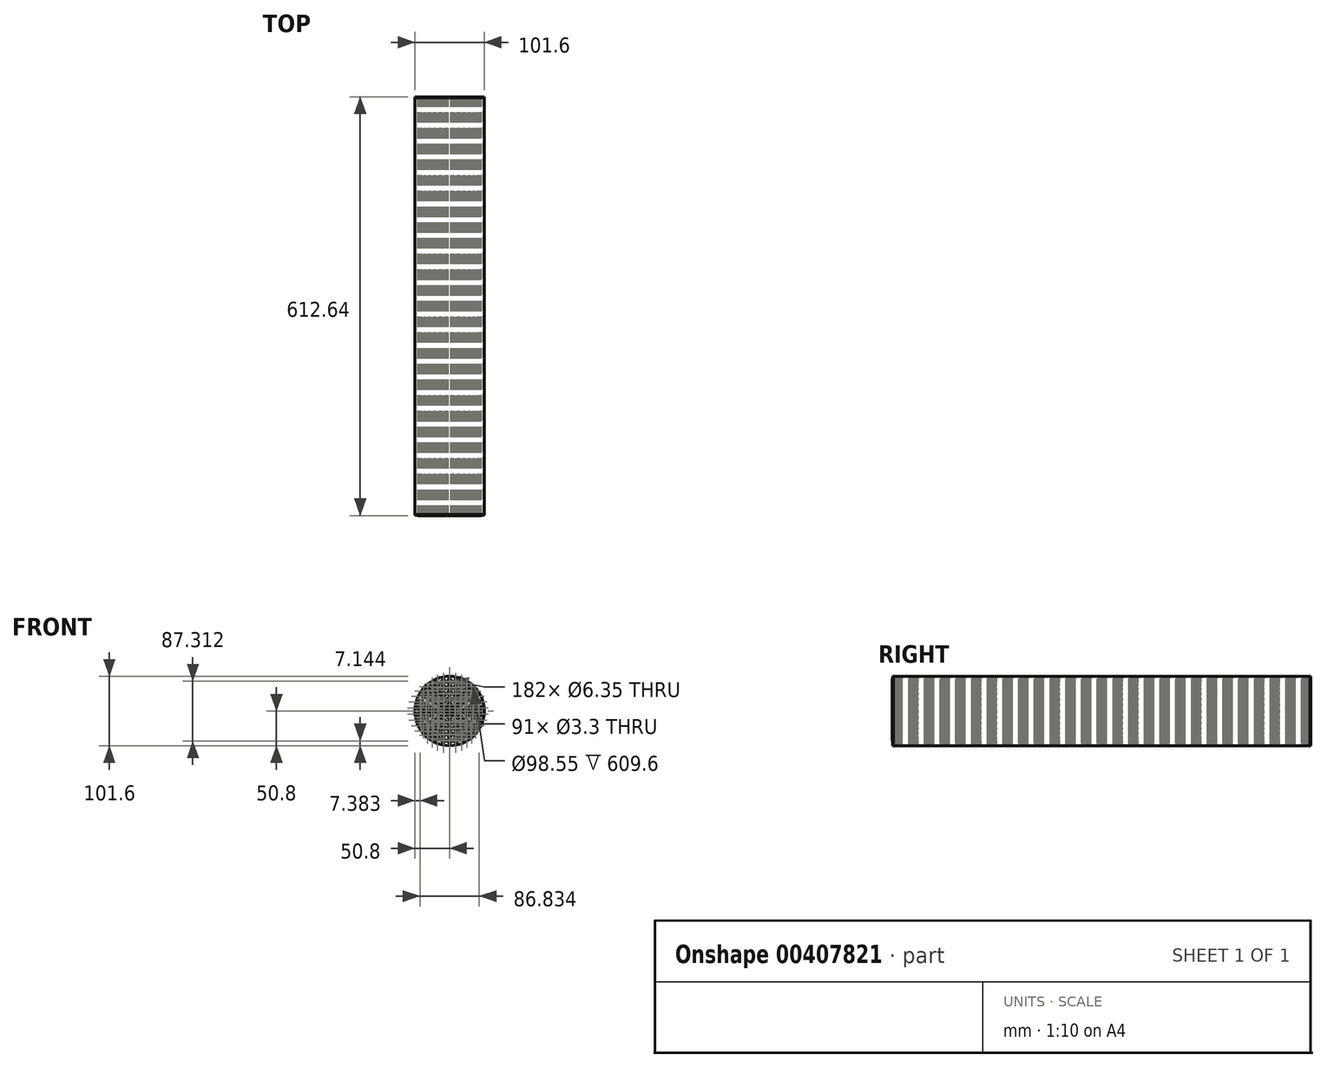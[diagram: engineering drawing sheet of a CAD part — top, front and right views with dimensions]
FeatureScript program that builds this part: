
annotation { "Feature Type Name" : "Feature", "Feature Type Description" : "" }
export const myFeature = defineFeature(function(context is Context, id is Id, definition is map)
    precondition{}
    {
        {
            var Q0;
            Q0=qCreatedBy(makeId("Front.planeOp"),FACE);
            var sketch = newSketch(context, id + "F0", { "sketchPlane" : qUnion([Q0])});
            skCircle(sketch, "E0", {"center": v(0, 0) * mm, "radius": 50.8 * mm});
            skCircle(sketch, "E1", {"center": v(0, 0) * mm, "radius": 3.18 * mm});
            skCircle(sketch, "E2", {"center": v(0, 8.73) * mm, "radius": 3.18 * mm});
            skCircle(sketch, "E3", {"center": v(0, 17.46) * mm, "radius": 3.18 * mm});
            skCircle(sketch, "E4", {"center": v(0, 26.2) * mm, "radius": 3.18 * mm});
            skCircle(sketch, "E5", {"center": v(0, 34.93) * mm, "radius": 3.18 * mm});
            skCircle(sketch, "E6", {"center": v(0, 43.66) * mm, "radius": 3.18 * mm});
            skCircle(sketch, "E7.0", {"center": v(0, 0) * mm, "radius": 49.28 * mm});
            skCircle(sketch, "E8.1.0", {"center": v(-7.56, 4.37) * mm, "radius": 3.18 * mm});
            skCircle(sketch, "E8.2.0", {"center": v(-7.56, -4.37) * mm, "radius": 3.18 * mm});
            skCircle(sketch, "E8.3.0", {"center": v(0, -8.73) * mm, "radius": 3.18 * mm});
            skCircle(sketch, "E8.4.0", {"center": v(7.56, -4.37) * mm, "radius": 3.18 * mm});
            skCircle(sketch, "E8.5.0", {"center": v(7.56, 4.37) * mm, "radius": 3.18 * mm});
            skCircle(sketch, "E9.1.0", {"center": v(-8.73, 15.12) * mm, "radius": 3.18 * mm});
            skCircle(sketch, "E9.2.0", {"center": v(-15.12, 8.73) * mm, "radius": 3.18 * mm});
            skCircle(sketch, "E9.3.0", {"center": v(-17.46, 0) * mm, "radius": 3.18 * mm});
            skCircle(sketch, "E9.4.0", {"center": v(-15.12, -8.73) * mm, "radius": 3.18 * mm});
            skCircle(sketch, "E9.5.0", {"center": v(-8.73, -15.12) * mm, "radius": 3.18 * mm});
            skCircle(sketch, "E9.6.0", {"center": v(0, -17.46) * mm, "radius": 3.18 * mm});
            skCircle(sketch, "E9.7.0", {"center": v(8.73, -15.12) * mm, "radius": 3.18 * mm});
            skCircle(sketch, "E9.8.0", {"center": v(15.12, -8.73) * mm, "radius": 3.18 * mm});
            skCircle(sketch, "E9.9.0", {"center": v(17.46, 0) * mm, "radius": 3.18 * mm});
            skCircle(sketch, "E9.10.0", {"center": v(15.12, 8.73) * mm, "radius": 3.18 * mm});
            skCircle(sketch, "E9.11.0", {"center": v(8.73, 15.12) * mm, "radius": 3.18 * mm});
            skCircle(sketch, "E10.1.0", {"center": v(-8.96, 24.61) * mm, "radius": 3.17 * mm});
            skCircle(sketch, "E10.2.0", {"center": v(-16.84, 20.07) * mm, "radius": 3.18 * mm});
            skCircle(sketch, "E10.3.0", {"center": v(-22.68, 13.1) * mm, "radius": 3.18 * mm});
            skCircle(sketch, "E10.4.0", {"center": v(-25.8, 4.55) * mm, "radius": 3.18 * mm});
            skCircle(sketch, "E10.5.0", {"center": v(-25.8, -4.55) * mm, "radius": 3.18 * mm});
            skCircle(sketch, "E10.6.0", {"center": v(-22.68, -13.1) * mm, "radius": 3.18 * mm});
            skCircle(sketch, "E10.7.0", {"center": v(-16.84, -20.07) * mm, "radius": 3.17 * mm});
            skCircle(sketch, "E10.8.0", {"center": v(-8.96, -24.61) * mm, "radius": 3.18 * mm});
            skCircle(sketch, "E10.9.0", {"center": v(0, -26.2) * mm, "radius": 3.17 * mm});
            skCircle(sketch, "E10.10.0", {"center": v(8.96, -24.61) * mm, "radius": 3.18 * mm});
            skCircle(sketch, "E10.11.0", {"center": v(16.84, -20.07) * mm, "radius": 3.18 * mm});
            skCircle(sketch, "E10.12.0", {"center": v(22.68, -13.1) * mm, "radius": 3.17 * mm});
            skCircle(sketch, "E10.13.0", {"center": v(25.8, -4.55) * mm, "radius": 3.17 * mm});
            skCircle(sketch, "E10.14.0", {"center": v(25.8, 4.55) * mm, "radius": 3.18 * mm});
            skCircle(sketch, "E10.15.0", {"center": v(22.68, 13.1) * mm, "radius": 3.18 * mm});
            skCircle(sketch, "E10.16.0", {"center": v(16.84, 20.07) * mm, "radius": 3.18 * mm});
            skCircle(sketch, "E10.17.0", {"center": v(8.96, 24.61) * mm, "radius": 3.18 * mm});
            skCircle(sketch, "E11.1.0", {"center": v(-9.04, 33.73) * mm, "radius": 3.18 * mm});
            skCircle(sketch, "E11.2.0", {"center": v(-17.46, 30.25) * mm, "radius": 3.18 * mm});
            skCircle(sketch, "E11.3.0", {"center": v(-24.7, 24.7) * mm, "radius": 3.18 * mm});
            skCircle(sketch, "E11.4.0", {"center": v(-30.25, 17.46) * mm, "radius": 3.18 * mm});
            skCircle(sketch, "E11.5.0", {"center": v(-33.73, 9.04) * mm, "radius": 3.18 * mm});
            skCircle(sketch, "E11.6.0", {"center": v(-34.93, 0) * mm, "radius": 3.18 * mm});
            skCircle(sketch, "E11.7.0", {"center": v(-33.73, -9.04) * mm, "radius": 3.18 * mm});
            skCircle(sketch, "E11.8.0", {"center": v(-30.25, -17.46) * mm, "radius": 3.18 * mm});
            skCircle(sketch, "E11.9.0", {"center": v(-24.7, -24.7) * mm, "radius": 3.18 * mm});
            skCircle(sketch, "E11.10.0", {"center": v(-17.46, -30.25) * mm, "radius": 3.18 * mm});
            skCircle(sketch, "E11.11.0", {"center": v(-9.04, -33.73) * mm, "radius": 3.18 * mm});
            skCircle(sketch, "E11.12.0", {"center": v(0, -34.93) * mm, "radius": 3.18 * mm});
            skCircle(sketch, "E11.13.0", {"center": v(9.04, -33.73) * mm, "radius": 3.18 * mm});
            skCircle(sketch, "E11.14.0", {"center": v(17.46, -30.25) * mm, "radius": 3.18 * mm});
            skCircle(sketch, "E11.15.0", {"center": v(24.7, -24.7) * mm, "radius": 3.18 * mm});
            skCircle(sketch, "E11.16.0", {"center": v(30.25, -17.46) * mm, "radius": 3.18 * mm});
            skCircle(sketch, "E11.17.0", {"center": v(33.73, -9.04) * mm, "radius": 3.18 * mm});
            skCircle(sketch, "E11.18.0", {"center": v(34.93, 0) * mm, "radius": 3.18 * mm});
            skCircle(sketch, "E11.19.0", {"center": v(33.73, 9.04) * mm, "radius": 3.18 * mm});
            skCircle(sketch, "E11.20.0", {"center": v(30.25, 17.46) * mm, "radius": 3.18 * mm});
            skCircle(sketch, "E11.21.0", {"center": v(24.7, 24.7) * mm, "radius": 3.18 * mm});
            skCircle(sketch, "E11.22.0", {"center": v(17.46, 30.25) * mm, "radius": 3.18 * mm});
            skCircle(sketch, "E11.23.0", {"center": v(9.04, 33.73) * mm, "radius": 3.18 * mm});
            skCircle(sketch, "E12.1.0", {"center": v(-9.08, 42.7) * mm, "radius": 3.18 * mm});
            skCircle(sketch, "E12.2.0", {"center": v(-17.76, 39.88) * mm, "radius": 3.18 * mm});
            skCircle(sketch, "E12.3.0", {"center": v(-25.66, 35.32) * mm, "radius": 3.18 * mm});
            skCircle(sketch, "E12.4.0", {"center": v(-32.44, 29.21) * mm, "radius": 3.17 * mm});
            skCircle(sketch, "E12.5.0", {"center": v(-37.8, 21.83) * mm, "radius": 3.18 * mm});
            skCircle(sketch, "E12.6.0", {"center": v(-41.52, 13.5) * mm, "radius": 3.18 * mm});
            skCircle(sketch, "E12.7.0", {"center": v(-43.42, 4.56) * mm, "radius": 3.18 * mm});
            skCircle(sketch, "E12.8.0", {"center": v(-43.42, -4.56) * mm, "radius": 3.18 * mm});
            skCircle(sketch, "E12.9.0", {"center": v(-41.52, -13.5) * mm, "radius": 3.18 * mm});
            skCircle(sketch, "E12.10.0", {"center": v(-37.8, -21.83) * mm, "radius": 3.18 * mm});
            skCircle(sketch, "E12.11.0", {"center": v(-32.44, -29.21) * mm, "radius": 3.18 * mm});
            skCircle(sketch, "E12.12.0", {"center": v(-25.66, -35.32) * mm, "radius": 3.18 * mm});
            skCircle(sketch, "E12.13.0", {"center": v(-17.76, -39.88) * mm, "radius": 3.18 * mm});
            skCircle(sketch, "E12.14.0", {"center": v(-9.08, -42.7) * mm, "radius": 3.18 * mm});
            skCircle(sketch, "E12.15.0", {"center": v(0, -43.66) * mm, "radius": 3.18 * mm});
            skCircle(sketch, "E12.16.0", {"center": v(9.08, -42.7) * mm, "radius": 3.18 * mm});
            skCircle(sketch, "E12.17.0", {"center": v(17.76, -39.88) * mm, "radius": 3.17 * mm});
            skCircle(sketch, "E12.18.0", {"center": v(25.66, -35.32) * mm, "radius": 3.18 * mm});
            skCircle(sketch, "E12.19.0", {"center": v(32.44, -29.21) * mm, "radius": 3.18 * mm});
            skCircle(sketch, "E12.20.0", {"center": v(37.8, -21.83) * mm, "radius": 3.18 * mm});
            skCircle(sketch, "E12.21.0", {"center": v(41.52, -13.5) * mm, "radius": 3.18 * mm});
            skCircle(sketch, "E12.22.0", {"center": v(43.42, -4.56) * mm, "radius": 3.18 * mm});
            skCircle(sketch, "E12.23.0", {"center": v(43.42, 4.56) * mm, "radius": 3.18 * mm});
            skCircle(sketch, "E12.24.0", {"center": v(41.52, 13.5) * mm, "radius": 3.18 * mm});
            skCircle(sketch, "E12.25.0", {"center": v(37.8, 21.83) * mm, "radius": 3.18 * mm});
            skCircle(sketch, "E12.26.0", {"center": v(32.44, 29.21) * mm, "radius": 3.18 * mm});
            skCircle(sketch, "E12.27.0", {"center": v(25.66, 35.32) * mm, "radius": 3.18 * mm});
            skCircle(sketch, "E12.28.0", {"center": v(17.76, 39.88) * mm, "radius": 3.18 * mm});
            skCircle(sketch, "E12.29.0", {"center": v(9.08, 42.7) * mm, "radius": 3.18 * mm});
            skSolve(sketch);
        }
        {
            var Q0;
            Q0=makeQuery(id+"F0.imprint","IMPRINT",FACE,{"disambiguationData":[TD([[makeQuery(id+"F0.imprint","IMPRINT",EDGE,{"derivedFrom":sQuery(id+"F0.wireOp",EDGE,"E0")}),1.0]])]});
            extrude(context, id + "F1", {"entities" : qUnion([Q0]), "depth" : 609.6 * mm});
        }
        {
            var Q0;
            Q0=makeQuery(id+"F0.imprint","IMPRINT",FACE,{"disambiguationData":[TD([[makeQuery(id+"F0.imprint","IMPRINT",EDGE,{"derivedFrom":sQuery(id+"F0.wireOp",EDGE,"E12.26.0")}),1.0]])]});
            var Q1;
            Q1=makeQuery(id+"F0.imprint","IMPRINT",FACE,{"disambiguationData":[TD([[makeQuery(id+"F0.imprint","IMPRINT",EDGE,{"derivedFrom":sQuery(id+"F0.wireOp",EDGE,"E10.12.0")}),1.0]])]});
            var Q2;
            Q2=makeQuery(id+"F0.imprint","IMPRINT",FACE,{"disambiguationData":[TD([[makeQuery(id+"F0.imprint","IMPRINT",EDGE,{"derivedFrom":sQuery(id+"F0.wireOp",EDGE,"E11.11.0")}),1.0]])]});
            var Q3;
            Q3=makeQuery(id+"F0.imprint","IMPRINT",FACE,{"disambiguationData":[TD([[makeQuery(id+"F0.imprint","IMPRINT",EDGE,{"derivedFrom":sQuery(id+"F0.wireOp",EDGE,"E11.10.0")}),1.0]])]});
            var Q4;
            Q4=makeQuery(id+"F0.imprint","IMPRINT",FACE,{"disambiguationData":[TD([[makeQuery(id+"F0.imprint","IMPRINT",EDGE,{"derivedFrom":sQuery(id+"F0.wireOp",EDGE,"E10.1.0")}),1.0]])]});
            var Q5;
            Q5=makeQuery(id+"F0.imprint","IMPRINT",FACE,{"disambiguationData":[TD([[makeQuery(id+"F0.imprint","IMPRINT",EDGE,{"derivedFrom":sQuery(id+"F0.wireOp",EDGE,"E12.10.0")}),1.0]])]});
            var Q6;
            Q6=makeQuery(id+"F0.imprint","IMPRINT",FACE,{"disambiguationData":[TD([[makeQuery(id+"F0.imprint","IMPRINT",EDGE,{"derivedFrom":sQuery(id+"F0.wireOp",EDGE,"E12.11.0")}),1.0]])]});
            var Q7;
            Q7=makeQuery(id+"F0.imprint","IMPRINT",FACE,{"disambiguationData":[TD([[makeQuery(id+"F0.imprint","IMPRINT",EDGE,{"derivedFrom":sQuery(id+"F0.wireOp",EDGE,"E11.8.0")}),1.0]])]});
            var Q8;
            Q8=makeQuery(id+"F0.imprint","IMPRINT",FACE,{"disambiguationData":[TD([[makeQuery(id+"F0.imprint","IMPRINT",EDGE,{"derivedFrom":sQuery(id+"F0.wireOp",EDGE,"E10.3.0")}),1.0]])]});
            var Q9;
            Q9=makeQuery(id+"F0.imprint","IMPRINT",FACE,{"disambiguationData":[TD([[makeQuery(id+"F0.imprint","IMPRINT",EDGE,{"derivedFrom":sQuery(id+"F0.wireOp",EDGE,"E12.17.0")}),1.0]])]});
            var Q10;
            Q10=makeQuery(id+"F0.imprint","IMPRINT",FACE,{"disambiguationData":[TD([[makeQuery(id+"F0.imprint","IMPRINT",EDGE,{"derivedFrom":sQuery(id+"F0.wireOp",EDGE,"E12.1.0")}),1.0]])]});
            var Q11;
            Q11=makeQuery(id+"F0.imprint","IMPRINT",FACE,{"disambiguationData":[TD([[makeQuery(id+"F0.imprint","IMPRINT",EDGE,{"derivedFrom":sQuery(id+"F0.wireOp",EDGE,"E10.13.0")}),1.0]])]});
            var Q12;
            Q12=makeQuery(id+"F0.imprint","IMPRINT",FACE,{"disambiguationData":[TD([[makeQuery(id+"F0.imprint","IMPRINT",EDGE,{"derivedFrom":sQuery(id+"F0.wireOp",EDGE,"E11.12.0")}),1.0]])]});
            var Q13;
            Q13=makeQuery(id+"F0.imprint","IMPRINT",FACE,{"disambiguationData":[TD([[makeQuery(id+"F0.imprint","IMPRINT",EDGE,{"derivedFrom":sQuery(id+"F0.wireOp",EDGE,"E12.14.0")}),1.0]])]});
            var Q14;
            Q14=makeQuery(id+"F0.imprint","IMPRINT",FACE,{"disambiguationData":[TD([[makeQuery(id+"F0.imprint","IMPRINT",EDGE,{"derivedFrom":sQuery(id+"F0.wireOp",EDGE,"E12.28.0")}),1.0]])]});
            var Q15;
            Q15=makeQuery(id+"F0.imprint","IMPRINT",FACE,{"disambiguationData":[TD([[makeQuery(id+"F0.imprint","IMPRINT",EDGE,{"derivedFrom":sQuery(id+"F0.wireOp",EDGE,"E12.12.0")}),1.0]])]});
            var Q16;
            Q16=makeQuery(id+"F0.imprint","IMPRINT",FACE,{"disambiguationData":[TD([[makeQuery(id+"F0.imprint","IMPRINT",EDGE,{"derivedFrom":sQuery(id+"F0.wireOp",EDGE,"E9.4.0")}),1.0]])]});
            var Q17;
            Q17=makeQuery(id+"F0.imprint","IMPRINT",FACE,{"disambiguationData":[TD([[makeQuery(id+"F0.imprint","IMPRINT",EDGE,{"derivedFrom":sQuery(id+"F0.wireOp",EDGE,"E12.6.0")}),1.0]])]});
            var Q18;
            Q18=makeQuery(id+"F0.imprint","IMPRINT",FACE,{"disambiguationData":[TD([[makeQuery(id+"F0.imprint","IMPRINT",EDGE,{"derivedFrom":sQuery(id+"F0.wireOp",EDGE,"E11.13.0")}),1.0]])]});
            var Q19;
            Q19=makeQuery(id+"F0.imprint","IMPRINT",FACE,{"disambiguationData":[TD([[makeQuery(id+"F0.imprint","IMPRINT",EDGE,{"derivedFrom":sQuery(id+"F0.wireOp",EDGE,"E10.7.0")}),1.0]])]});
            var Q20;
            Q20=makeQuery(id+"F0.imprint","IMPRINT",FACE,{"disambiguationData":[TD([[makeQuery(id+"F0.imprint","IMPRINT",EDGE,{"derivedFrom":sQuery(id+"F0.wireOp",EDGE,"E10.10.0")}),1.0]])]});
            var Q21;
            Q21=makeQuery(id+"F0.imprint","IMPRINT",FACE,{"disambiguationData":[TD([[makeQuery(id+"F0.imprint","IMPRINT",EDGE,{"derivedFrom":sQuery(id+"F0.wireOp",EDGE,"E12.20.0")}),1.0]])]});
            var Q22;
            Q22=makeQuery(id+"F0.imprint","IMPRINT",FACE,{"disambiguationData":[TD([[makeQuery(id+"F0.imprint","IMPRINT",EDGE,{"derivedFrom":sQuery(id+"F0.wireOp",EDGE,"E10.11.0")}),1.0]])]});
            var Q23;
            Q23=makeQuery(id+"F0.imprint","IMPRINT",FACE,{"disambiguationData":[TD([[makeQuery(id+"F0.imprint","IMPRINT",EDGE,{"derivedFrom":sQuery(id+"F0.wireOp",EDGE,"E10.14.0")}),1.0]])]});
            var Q24;
            Q24=makeQuery(id+"F0.imprint","IMPRINT",FACE,{"disambiguationData":[TD([[makeQuery(id+"F0.imprint","IMPRINT",EDGE,{"derivedFrom":sQuery(id+"F0.wireOp",EDGE,"E12.23.0")}),1.0]])]});
            var Q25;
            Q25=makeQuery(id+"F0.imprint","IMPRINT",FACE,{"disambiguationData":[TD([[makeQuery(id+"F0.imprint","IMPRINT",EDGE,{"derivedFrom":sQuery(id+"F0.wireOp",EDGE,"E11.9.0")}),1.0]])]});
            var Q26;
            Q26=makeQuery(id+"F0.imprint","IMPRINT",FACE,{"disambiguationData":[TD([[makeQuery(id+"F0.imprint","IMPRINT",EDGE,{"derivedFrom":sQuery(id+"F0.wireOp",EDGE,"E11.7.0")}),1.0]])]});
            var Q27;
            Q27=makeQuery(id+"F0.imprint","IMPRINT",FACE,{"disambiguationData":[TD([[makeQuery(id+"F0.imprint","IMPRINT",EDGE,{"derivedFrom":sQuery(id+"F0.wireOp",EDGE,"E10.8.0")}),1.0]])]});
            var Q28;
            Q28=makeQuery(id+"F0.imprint","IMPRINT",FACE,{"disambiguationData":[TD([[makeQuery(id+"F0.imprint","IMPRINT",EDGE,{"derivedFrom":sQuery(id+"F0.wireOp",EDGE,"E10.16.0")}),1.0]])]});
            var Q29;
            Q29=makeQuery(id+"F0.imprint","IMPRINT",FACE,{"disambiguationData":[TD([[makeQuery(id+"F0.imprint","IMPRINT",EDGE,{"derivedFrom":sQuery(id+"F0.wireOp",EDGE,"E9.2.0")}),1.0]])]});
            var Q30;
            Q30=makeQuery(id+"F0.imprint","IMPRINT",FACE,{"disambiguationData":[TD([[makeQuery(id+"F0.imprint","IMPRINT",EDGE,{"derivedFrom":sQuery(id+"F0.wireOp",EDGE,"E11.17.0")}),1.0]])]});
            var Q31;
            Q31=makeQuery(id+"F0.imprint","IMPRINT",FACE,{"disambiguationData":[TD([[makeQuery(id+"F0.imprint","IMPRINT",EDGE,{"derivedFrom":sQuery(id+"F0.wireOp",EDGE,"E12.29.0")}),1.0]])]});
            var Q32;
            Q32=makeQuery(id+"F0.imprint","IMPRINT",FACE,{"disambiguationData":[TD([[makeQuery(id+"F0.imprint","IMPRINT",EDGE,{"derivedFrom":sQuery(id+"F0.wireOp",EDGE,"E2")}),1.0]])]});
            var Q33;
            Q33=makeQuery(id+"F0.imprint","IMPRINT",FACE,{"disambiguationData":[TD([[makeQuery(id+"F0.imprint","IMPRINT",EDGE,{"derivedFrom":sQuery(id+"F0.wireOp",EDGE,"E5")}),1.0]])]});
            var Q34;
            Q34=makeQuery(id+"F0.imprint","IMPRINT",FACE,{"disambiguationData":[TD([[makeQuery(id+"F0.imprint","IMPRINT",EDGE,{"derivedFrom":sQuery(id+"F0.wireOp",EDGE,"E6")}),1.0]])]});
            var Q35;
            Q35=makeQuery(id+"F0.imprint","IMPRINT",FACE,{"disambiguationData":[TD([[makeQuery(id+"F0.imprint","IMPRINT",EDGE,{"derivedFrom":sQuery(id+"F0.wireOp",EDGE,"E8.2.0")}),1.0]])]});
            var Q36;
            Q36=makeQuery(id+"F0.imprint","IMPRINT",FACE,{"disambiguationData":[TD([[makeQuery(id+"F0.imprint","IMPRINT",EDGE,{"derivedFrom":sQuery(id+"F0.wireOp",EDGE,"E8.1.0")}),1.0]])]});
            var Q37;
            Q37=makeQuery(id+"F0.imprint","IMPRINT",FACE,{"disambiguationData":[TD([[makeQuery(id+"F0.imprint","IMPRINT",EDGE,{"derivedFrom":sQuery(id+"F0.wireOp",EDGE,"E8.5.0")}),1.0]])]});
            var Q38;
            Q38=makeQuery(id+"F0.imprint","IMPRINT",FACE,{"disambiguationData":[TD([[makeQuery(id+"F0.imprint","IMPRINT",EDGE,{"derivedFrom":sQuery(id+"F0.wireOp",EDGE,"E9.1.0")}),1.0]])]});
            var Q39;
            Q39=makeQuery(id+"F0.imprint","IMPRINT",FACE,{"disambiguationData":[TD([[makeQuery(id+"F0.imprint","IMPRINT",EDGE,{"derivedFrom":sQuery(id+"F0.wireOp",EDGE,"E9.6.0")}),1.0]])]});
            var Q40;
            Q40=makeQuery(id+"F0.imprint","IMPRINT",FACE,{"disambiguationData":[TD([[makeQuery(id+"F0.imprint","IMPRINT",EDGE,{"derivedFrom":sQuery(id+"F0.wireOp",EDGE,"E12.25.0")}),1.0]])]});
            var Q41;
            Q41=makeQuery(id+"F0.imprint","IMPRINT",FACE,{"disambiguationData":[TD([[makeQuery(id+"F0.imprint","IMPRINT",EDGE,{"derivedFrom":sQuery(id+"F0.wireOp",EDGE,"E11.16.0")}),1.0]])]});
            var Q42;
            Q42=makeQuery(id+"F0.imprint","IMPRINT",FACE,{"disambiguationData":[TD([[makeQuery(id+"F0.imprint","IMPRINT",EDGE,{"derivedFrom":sQuery(id+"F0.wireOp",EDGE,"E11.18.0")}),1.0]])]});
            var Q43;
            Q43=makeQuery(id+"F0.imprint","IMPRINT",FACE,{"disambiguationData":[TD([[makeQuery(id+"F0.imprint","IMPRINT",EDGE,{"derivedFrom":sQuery(id+"F0.wireOp",EDGE,"E11.21.0")}),1.0]])]});
            var Q44;
            Q44=makeQuery(id+"F0.imprint","IMPRINT",FACE,{"disambiguationData":[TD([[makeQuery(id+"F0.imprint","IMPRINT",EDGE,{"derivedFrom":sQuery(id+"F0.wireOp",EDGE,"E12.27.0")}),1.0]])]});
            var Q45;
            Q45=makeQuery(id+"F0.imprint","IMPRINT",FACE,{"disambiguationData":[TD([[makeQuery(id+"F0.imprint","IMPRINT",EDGE,{"derivedFrom":sQuery(id+"F0.wireOp",EDGE,"E9.8.0")}),1.0]])]});
            var Q46;
            Q46=makeQuery(id+"F0.imprint","IMPRINT",FACE,{"disambiguationData":[TD([[makeQuery(id+"F0.imprint","IMPRINT",EDGE,{"derivedFrom":sQuery(id+"F0.wireOp",EDGE,"E12.21.0")}),1.0]])]});
            var Q47;
            Q47=makeQuery(id+"F0.imprint","IMPRINT",FACE,{"disambiguationData":[TD([[makeQuery(id+"F0.imprint","IMPRINT",EDGE,{"derivedFrom":sQuery(id+"F0.wireOp",EDGE,"E12.5.0")}),1.0]])]});
            var Q48;
            Q48=makeQuery(id+"F0.imprint","IMPRINT",FACE,{"disambiguationData":[TD([[makeQuery(id+"F0.imprint","IMPRINT",EDGE,{"derivedFrom":sQuery(id+"F0.wireOp",EDGE,"E12.8.0")}),1.0]])]});
            var Q49;
            Q49=makeQuery(id+"F0.imprint","IMPRINT",FACE,{"disambiguationData":[TD([[makeQuery(id+"F0.imprint","IMPRINT",EDGE,{"derivedFrom":sQuery(id+"F0.wireOp",EDGE,"E12.24.0")}),1.0]])]});
            var Q50;
            Q50=makeQuery(id+"F0.imprint","IMPRINT",FACE,{"disambiguationData":[TD([[makeQuery(id+"F0.imprint","IMPRINT",EDGE,{"derivedFrom":sQuery(id+"F0.wireOp",EDGE,"E9.9.0")}),1.0]])]});
            var Q51;
            Q51=makeQuery(id+"F0.imprint","IMPRINT",FACE,{"disambiguationData":[TD([[makeQuery(id+"F0.imprint","IMPRINT",EDGE,{"derivedFrom":sQuery(id+"F0.wireOp",EDGE,"E12.22.0")}),1.0]])]});
            var Q52;
            Q52=makeQuery(id+"F0.imprint","IMPRINT",FACE,{"disambiguationData":[TD([[makeQuery(id+"F0.imprint","IMPRINT",EDGE,{"derivedFrom":sQuery(id+"F0.wireOp",EDGE,"E11.22.0")}),1.0]])]});
            var Q53;
            Q53=makeQuery(id+"F0.imprint","IMPRINT",FACE,{"disambiguationData":[TD([[makeQuery(id+"F0.imprint","IMPRINT",EDGE,{"derivedFrom":sQuery(id+"F0.wireOp",EDGE,"E11.6.0")}),1.0]])]});
            var Q54;
            Q54=makeQuery(id+"F0.imprint","IMPRINT",FACE,{"disambiguationData":[TD([[makeQuery(id+"F0.imprint","IMPRINT",EDGE,{"derivedFrom":sQuery(id+"F0.wireOp",EDGE,"E10.5.0")}),1.0]])]});
            var Q55;
            Q55=makeQuery(id+"F0.imprint","IMPRINT",FACE,{"disambiguationData":[TD([[makeQuery(id+"F0.imprint","IMPRINT",EDGE,{"derivedFrom":sQuery(id+"F0.wireOp",EDGE,"E10.9.0")}),1.0]])]});
            var Q56;
            Q56=makeQuery(id+"F0.imprint","IMPRINT",FACE,{"disambiguationData":[TD([[makeQuery(id+"F0.imprint","IMPRINT",EDGE,{"derivedFrom":sQuery(id+"F0.wireOp",EDGE,"E9.10.0")}),1.0]])]});
            var Q57;
            Q57=makeQuery(id+"F0.imprint","IMPRINT",FACE,{"disambiguationData":[TD([[makeQuery(id+"F0.imprint","IMPRINT",EDGE,{"derivedFrom":sQuery(id+"F0.wireOp",EDGE,"E12.13.0")}),1.0]])]});
            var Q58;
            Q58=makeQuery(id+"F0.imprint","IMPRINT",FACE,{"disambiguationData":[TD([[makeQuery(id+"F0.imprint","IMPRINT",EDGE,{"derivedFrom":sQuery(id+"F0.wireOp",EDGE,"E12.16.0")}),1.0]])]});
            var Q59;
            Q59=makeQuery(id+"F0.imprint","IMPRINT",FACE,{"disambiguationData":[TD([[makeQuery(id+"F0.imprint","IMPRINT",EDGE,{"derivedFrom":sQuery(id+"F0.wireOp",EDGE,"E11.23.0")}),1.0]])]});
            var Q60;
            Q60=makeQuery(id+"F0.imprint","IMPRINT",FACE,{"disambiguationData":[TD([[makeQuery(id+"F0.imprint","IMPRINT",EDGE,{"derivedFrom":sQuery(id+"F0.wireOp",EDGE,"E11.14.0")}),1.0]])]});
            var Q61;
            Q61=makeQuery(id+"F0.imprint","IMPRINT",FACE,{"disambiguationData":[TD([[makeQuery(id+"F0.imprint","IMPRINT",EDGE,{"derivedFrom":sQuery(id+"F0.wireOp",EDGE,"E10.15.0")}),1.0]])]});
            var Q62;
            Q62=makeQuery(id+"F0.imprint","IMPRINT",FACE,{"disambiguationData":[TD([[makeQuery(id+"F0.imprint","IMPRINT",EDGE,{"derivedFrom":sQuery(id+"F0.wireOp",EDGE,"E10.6.0")}),1.0]])]});
            var Q63;
            Q63=makeQuery(id+"F0.imprint","IMPRINT",FACE,{"disambiguationData":[TD([[makeQuery(id+"F0.imprint","IMPRINT",EDGE,{"derivedFrom":sQuery(id+"F0.wireOp",EDGE,"E11.5.0")}),1.0]])]});
            var Q64;
            Q64=makeQuery(id+"F0.imprint","IMPRINT",FACE,{"disambiguationData":[TD([[makeQuery(id+"F0.imprint","IMPRINT",EDGE,{"derivedFrom":sQuery(id+"F0.wireOp",EDGE,"E12.19.0")}),1.0]])]});
            var Q65;
            Q65=makeQuery(id+"F0.imprint","IMPRINT",FACE,{"disambiguationData":[TD([[makeQuery(id+"F0.imprint","IMPRINT",EDGE,{"derivedFrom":sQuery(id+"F0.wireOp",EDGE,"E11.19.0")}),1.0]])]});
            var Q66;
            Q66=makeQuery(id+"F0.imprint","IMPRINT",FACE,{"disambiguationData":[TD([[makeQuery(id+"F0.imprint","IMPRINT",EDGE,{"derivedFrom":sQuery(id+"F0.wireOp",EDGE,"E11.2.0")}),1.0]])]});
            var Q67;
            Q67=makeQuery(id+"F0.imprint","IMPRINT",FACE,{"disambiguationData":[TD([[makeQuery(id+"F0.imprint","IMPRINT",EDGE,{"derivedFrom":sQuery(id+"F0.wireOp",EDGE,"E11.3.0")}),1.0]])]});
            var Q68;
            Q68=makeQuery(id+"F0.imprint","IMPRINT",FACE,{"disambiguationData":[TD([[makeQuery(id+"F0.imprint","IMPRINT",EDGE,{"derivedFrom":sQuery(id+"F0.wireOp",EDGE,"E10.4.0")}),1.0]])]});
            var Q69;
            Q69=makeQuery(id+"F0.imprint","IMPRINT",FACE,{"disambiguationData":[TD([[makeQuery(id+"F0.imprint","IMPRINT",EDGE,{"derivedFrom":sQuery(id+"F0.wireOp",EDGE,"E11.15.0")}),1.0]])]});
            var Q70;
            Q70=makeQuery(id+"F0.imprint","IMPRINT",FACE,{"disambiguationData":[TD([[makeQuery(id+"F0.imprint","IMPRINT",EDGE,{"derivedFrom":sQuery(id+"F0.wireOp",EDGE,"E9.11.0")}),1.0]])]});
            var Q71;
            Q71=makeQuery(id+"F0.imprint","IMPRINT",FACE,{"disambiguationData":[TD([[makeQuery(id+"F0.imprint","IMPRINT",EDGE,{"derivedFrom":sQuery(id+"F0.wireOp",EDGE,"E12.3.0")}),1.0]])]});
            var Q72;
            Q72=makeQuery(id+"F0.imprint","IMPRINT",FACE,{"disambiguationData":[TD([[makeQuery(id+"F0.imprint","IMPRINT",EDGE,{"derivedFrom":sQuery(id+"F0.wireOp",EDGE,"E9.3.0")}),1.0]])]});
            var Q73;
            Q73=makeQuery(id+"F0.imprint","IMPRINT",FACE,{"disambiguationData":[TD([[makeQuery(id+"F0.imprint","IMPRINT",EDGE,{"derivedFrom":sQuery(id+"F0.wireOp",EDGE,"E9.5.0")}),1.0]])]});
            var Q74;
            Q74=makeQuery(id+"F0.imprint","IMPRINT",FACE,{"disambiguationData":[TD([[makeQuery(id+"F0.imprint","IMPRINT",EDGE,{"derivedFrom":sQuery(id+"F0.wireOp",EDGE,"E12.18.0")}),1.0]])]});
            var Q75;
            Q75=makeQuery(id+"F0.imprint","IMPRINT",FACE,{"disambiguationData":[TD([[makeQuery(id+"F0.imprint","IMPRINT",EDGE,{"derivedFrom":sQuery(id+"F0.wireOp",EDGE,"E12.2.0")}),1.0]])]});
            var Q76;
            Q76=makeQuery(id+"F0.imprint","IMPRINT",FACE,{"disambiguationData":[TD([[makeQuery(id+"F0.imprint","IMPRINT",EDGE,{"derivedFrom":sQuery(id+"F0.wireOp",EDGE,"E12.15.0")}),1.0]])]});
            var Q77;
            Q77=makeQuery(id+"F0.imprint","IMPRINT",FACE,{"disambiguationData":[TD([[makeQuery(id+"F0.imprint","IMPRINT",EDGE,{"derivedFrom":sQuery(id+"F0.wireOp",EDGE,"E11.20.0")}),1.0]])]});
            var Q78;
            Q78=makeQuery(id+"F0.imprint","IMPRINT",FACE,{"disambiguationData":[TD([[makeQuery(id+"F0.imprint","IMPRINT",EDGE,{"derivedFrom":sQuery(id+"F0.wireOp",EDGE,"E11.4.0")}),1.0]])]});
            var Q79;
            Q79=makeQuery(id+"F0.imprint","IMPRINT",FACE,{"disambiguationData":[TD([[makeQuery(id+"F0.imprint","IMPRINT",EDGE,{"derivedFrom":sQuery(id+"F0.wireOp",EDGE,"E9.7.0")}),1.0]])]});
            var Q80;
            Q80=makeQuery(id+"F0.imprint","IMPRINT",FACE,{"disambiguationData":[TD([[makeQuery(id+"F0.imprint","IMPRINT",EDGE,{"derivedFrom":sQuery(id+"F0.wireOp",EDGE,"E1")}),1.0]])]});
            var Q81;
            Q81=makeQuery(id+"F0.imprint","IMPRINT",FACE,{"disambiguationData":[TD([[makeQuery(id+"F0.imprint","IMPRINT",EDGE,{"derivedFrom":sQuery(id+"F0.wireOp",EDGE,"E12.7.0")}),1.0]])]});
            var Q82;
            Q82=makeQuery(id+"F0.imprint","IMPRINT",FACE,{"disambiguationData":[TD([[makeQuery(id+"F0.imprint","IMPRINT",EDGE,{"derivedFrom":sQuery(id+"F0.wireOp",EDGE,"E4")}),1.0]])]});
            var Q83;
            Q83=makeQuery(id+"F0.imprint","IMPRINT",FACE,{"disambiguationData":[TD([[makeQuery(id+"F0.imprint","IMPRINT",EDGE,{"derivedFrom":sQuery(id+"F0.wireOp",EDGE,"E3")}),1.0]])]});
            var Q84;
            Q84=makeQuery(id+"F0.imprint","IMPRINT",FACE,{"disambiguationData":[TD([[makeQuery(id+"F0.imprint","IMPRINT",EDGE,{"derivedFrom":sQuery(id+"F0.wireOp",EDGE,"E8.3.0")}),1.0]])]});
            var Q85;
            Q85=makeQuery(id+"F0.imprint","IMPRINT",FACE,{"disambiguationData":[TD([[makeQuery(id+"F0.imprint","IMPRINT",EDGE,{"derivedFrom":sQuery(id+"F0.wireOp",EDGE,"E12.4.0")}),1.0]])]});
            var Q86;
            Q86=makeQuery(id+"F0.imprint","IMPRINT",FACE,{"disambiguationData":[TD([[makeQuery(id+"F0.imprint","IMPRINT",EDGE,{"derivedFrom":sQuery(id+"F0.wireOp",EDGE,"E8.4.0")}),1.0]])]});
            var Q87;
            Q87=makeQuery(id+"F0.imprint","IMPRINT",FACE,{"disambiguationData":[TD([[makeQuery(id+"F0.imprint","IMPRINT",EDGE,{"derivedFrom":sQuery(id+"F0.wireOp",EDGE,"E11.1.0")}),1.0]])]});
            var Q88;
            Q88=makeQuery(id+"F0.imprint","IMPRINT",FACE,{"disambiguationData":[TD([[makeQuery(id+"F0.imprint","IMPRINT",EDGE,{"derivedFrom":sQuery(id+"F0.wireOp",EDGE,"E10.17.0")}),1.0]])]});
            var Q89;
            Q89=makeQuery(id+"F0.imprint","IMPRINT",FACE,{"disambiguationData":[TD([[makeQuery(id+"F0.imprint","IMPRINT",EDGE,{"derivedFrom":sQuery(id+"F0.wireOp",EDGE,"E12.9.0")}),1.0]])]});
            var Q90;
            Q90=makeQuery(id+"F0.imprint","IMPRINT",FACE,{"disambiguationData":[TD([[makeQuery(id+"F0.imprint","IMPRINT",EDGE,{"derivedFrom":sQuery(id+"F0.wireOp",EDGE,"E10.2.0")}),1.0]])]});
            extrude(context, id + "F2", {"entities" : qUnion([Q0, Q1, Q2, Q3, Q4, Q5, Q6, Q7, Q8, Q9, Q10, Q11, Q12, Q13, Q14, Q15, Q16, Q17, Q18, Q19, Q20, Q21, Q22, Q23, Q24, Q25, Q26, Q27, Q28, Q29, Q30, Q31, Q32, Q33, Q34, Q35, Q36, Q37, Q38, Q39, Q40, Q41, Q42, Q43, Q44, Q45, Q46, Q47, Q48, Q49, Q50, Q51, Q52, Q53, Q54, Q55, Q56, Q57, Q58, Q59, Q60, Q61, Q62, Q63, Q64, Q65, Q66, Q67, Q68, Q69, Q70, Q71, Q72, Q73, Q74, Q75, Q76, Q77, Q78, Q79, Q80, Q81, Q82, Q83, Q84, Q85, Q86, Q87, Q88, Q89, Q90]), "depth" : 611.12 * mm, "hasSecondDirection" : true, "secondDirectionOppositeDirection" : true, "secondDirectionDepth" : 1.52 * mm});
        }
        {
            var Q0;
            Q0=makeQuery(id+"F2.opExtrude","CAP_FACE",FACE,{"disambiguationData":[OSD([sQuery(id+"F0.wireOp",EDGE,"E12.15.0")])],"isStart":false});
            var Q1;
            Q1=makeQuery(id+"F2.opExtrude","CAP_FACE",FACE,{"disambiguationData":[OSD([sQuery(id+"F0.wireOp",EDGE,"E12.14.0")])],"isStart":false});
            var Q2;
            Q2=makeQuery(id+"F2.opExtrude","CAP_FACE",FACE,{"disambiguationData":[OSD([sQuery(id+"F0.wireOp",EDGE,"E12.13.0")])],"isStart":false});
            var Q3;
            Q3=makeQuery(id+"F2.opExtrude","CAP_FACE",FACE,{"disambiguationData":[OSD([sQuery(id+"F0.wireOp",EDGE,"E12.12.0")])],"isStart":false});
            var Q4;
            Q4=makeQuery(id+"F2.opExtrude","CAP_FACE",FACE,{"disambiguationData":[OSD([sQuery(id+"F0.wireOp",EDGE,"E12.11.0")])],"isStart":false});
            var Q5;
            Q5=makeQuery(id+"F2.opExtrude","CAP_FACE",FACE,{"disambiguationData":[OSD([sQuery(id+"F0.wireOp",EDGE,"E12.10.0")])],"isStart":false});
            var Q6;
            Q6=makeQuery(id+"F2.opExtrude","CAP_FACE",FACE,{"disambiguationData":[OSD([sQuery(id+"F0.wireOp",EDGE,"E12.9.0")])],"isStart":false});
            var Q7;
            Q7=makeQuery(id+"F2.opExtrude","CAP_FACE",FACE,{"disambiguationData":[OSD([sQuery(id+"F0.wireOp",EDGE,"E12.8.0")])],"isStart":false});
            var Q8;
            Q8=makeQuery(id+"F2.opExtrude","CAP_FACE",FACE,{"disambiguationData":[OSD([sQuery(id+"F0.wireOp",EDGE,"E12.7.0")])],"isStart":false});
            var Q9;
            Q9=makeQuery(id+"F2.opExtrude","CAP_FACE",FACE,{"disambiguationData":[OSD([sQuery(id+"F0.wireOp",EDGE,"E12.6.0")])],"isStart":false});
            var Q10;
            Q10=makeQuery(id+"F2.opExtrude","CAP_FACE",FACE,{"disambiguationData":[OSD([sQuery(id+"F0.wireOp",EDGE,"E12.5.0")])],"isStart":false});
            var Q11;
            Q11=makeQuery(id+"F2.opExtrude","CAP_FACE",FACE,{"disambiguationData":[OSD([sQuery(id+"F0.wireOp",EDGE,"E12.4.0")])],"isStart":false});
            var Q12;
            Q12=makeQuery(id+"F2.opExtrude","CAP_FACE",FACE,{"disambiguationData":[OSD([sQuery(id+"F0.wireOp",EDGE,"E12.3.0")])],"isStart":false});
            var Q13;
            Q13=makeQuery(id+"F2.opExtrude","CAP_FACE",FACE,{"disambiguationData":[OSD([sQuery(id+"F0.wireOp",EDGE,"E12.2.0")])],"isStart":false});
            var Q14;
            Q14=makeQuery(id+"F2.opExtrude","CAP_FACE",FACE,{"disambiguationData":[OSD([sQuery(id+"F0.wireOp",EDGE,"E12.1.0")])],"isStart":false});
            var Q15;
            Q15=makeQuery(id+"F2.opExtrude","CAP_FACE",FACE,{"disambiguationData":[OSD([sQuery(id+"F0.wireOp",EDGE,"E11.8.0")])],"isStart":false});
            var Q16;
            Q16=makeQuery(id+"F2.opExtrude","CAP_FACE",FACE,{"disambiguationData":[OSD([sQuery(id+"F0.wireOp",EDGE,"E11.7.0")])],"isStart":false});
            var Q17;
            Q17=makeQuery(id+"F2.opExtrude","CAP_FACE",FACE,{"disambiguationData":[OSD([sQuery(id+"F0.wireOp",EDGE,"E11.6.0")])],"isStart":false});
            var Q18;
            Q18=makeQuery(id+"F2.opExtrude","CAP_FACE",FACE,{"disambiguationData":[OSD([sQuery(id+"F0.wireOp",EDGE,"E11.5.0")])],"isStart":false});
            var Q19;
            Q19=makeQuery(id+"F2.opExtrude","CAP_FACE",FACE,{"disambiguationData":[OSD([sQuery(id+"F0.wireOp",EDGE,"E11.4.0")])],"isStart":false});
            var Q20;
            Q20=makeQuery(id+"F2.opExtrude","CAP_FACE",FACE,{"disambiguationData":[OSD([sQuery(id+"F0.wireOp",EDGE,"E11.3.0")])],"isStart":false});
            var Q21;
            Q21=makeQuery(id+"F2.opExtrude","CAP_FACE",FACE,{"disambiguationData":[OSD([sQuery(id+"F0.wireOp",EDGE,"E6")])],"isStart":false});
            var Q22;
            Q22=makeQuery(id+"F2.opExtrude","CAP_FACE",FACE,{"disambiguationData":[OSD([sQuery(id+"F0.wireOp",EDGE,"E12.16.0")])],"isStart":false});
            var Q23;
            Q23=makeQuery(id+"F2.opExtrude","CAP_FACE",FACE,{"disambiguationData":[OSD([sQuery(id+"F0.wireOp",EDGE,"E11.11.0")])],"isStart":false});
            var Q24;
            Q24=makeQuery(id+"F2.opExtrude","CAP_FACE",FACE,{"disambiguationData":[OSD([sQuery(id+"F0.wireOp",EDGE,"E11.1.0")])],"isStart":false});
            var Q25;
            Q25=makeQuery(id+"F2.opExtrude","CAP_FACE",FACE,{"disambiguationData":[OSD([sQuery(id+"F0.wireOp",EDGE,"E12.28.0")])],"isStart":false});
            var Q26;
            Q26=makeQuery(id+"F2.opExtrude","CAP_FACE",FACE,{"disambiguationData":[OSD([sQuery(id+"F0.wireOp",EDGE,"E12.17.0")])],"isStart":false});
            var Q27;
            Q27=makeQuery(id+"F2.opExtrude","CAP_FACE",FACE,{"disambiguationData":[OSD([sQuery(id+"F0.wireOp",EDGE,"E11.12.0")])],"isStart":false});
            var Q28;
            Q28=makeQuery(id+"F2.opExtrude","CAP_FACE",FACE,{"disambiguationData":[OSD([sQuery(id+"F0.wireOp",EDGE,"E11.10.0")])],"isStart":false});
            var Q29;
            Q29=makeQuery(id+"F2.opExtrude","CAP_FACE",FACE,{"disambiguationData":[OSD([sQuery(id+"F0.wireOp",EDGE,"E11.9.0")])],"isStart":false});
            var Q30;
            Q30=makeQuery(id+"F2.opExtrude","CAP_FACE",FACE,{"disambiguationData":[OSD([sQuery(id+"F0.wireOp",EDGE,"E11.2.0")])],"isStart":false});
            var Q31;
            Q31=makeQuery(id+"F2.opExtrude","CAP_FACE",FACE,{"disambiguationData":[OSD([sQuery(id+"F0.wireOp",EDGE,"E10.7.0")])],"isStart":false});
            var Q32;
            Q32=makeQuery(id+"F2.opExtrude","CAP_FACE",FACE,{"disambiguationData":[OSD([sQuery(id+"F0.wireOp",EDGE,"E10.6.0")])],"isStart":false});
            var Q33;
            Q33=makeQuery(id+"F2.opExtrude","CAP_FACE",FACE,{"disambiguationData":[OSD([sQuery(id+"F0.wireOp",EDGE,"E10.5.0")])],"isStart":false});
            var Q34;
            Q34=makeQuery(id+"F2.opExtrude","CAP_FACE",FACE,{"disambiguationData":[OSD([sQuery(id+"F0.wireOp",EDGE,"E10.4.0")])],"isStart":false});
            var Q35;
            Q35=makeQuery(id+"F2.opExtrude","CAP_FACE",FACE,{"disambiguationData":[OSD([sQuery(id+"F0.wireOp",EDGE,"E10.3.0")])],"isStart":false});
            var Q36;
            Q36=makeQuery(id+"F2.opExtrude","CAP_FACE",FACE,{"disambiguationData":[OSD([sQuery(id+"F0.wireOp",EDGE,"E10.2.0")])],"isStart":false});
            var Q37;
            Q37=makeQuery(id+"F2.opExtrude","CAP_FACE",FACE,{"disambiguationData":[OSD([sQuery(id+"F0.wireOp",EDGE,"E10.1.0")])],"isStart":false});
            var Q38;
            Q38=makeQuery(id+"F2.opExtrude","CAP_FACE",FACE,{"disambiguationData":[OSD([sQuery(id+"F0.wireOp",EDGE,"E9.4.0")])],"isStart":false});
            var Q39;
            Q39=makeQuery(id+"F2.opExtrude","CAP_FACE",FACE,{"disambiguationData":[OSD([sQuery(id+"F0.wireOp",EDGE,"E9.3.0")])],"isStart":false});
            var Q40;
            Q40=makeQuery(id+"F2.opExtrude","CAP_FACE",FACE,{"disambiguationData":[OSD([sQuery(id+"F0.wireOp",EDGE,"E9.2.0")])],"isStart":false});
            var Q41;
            Q41=makeQuery(id+"F2.opExtrude","CAP_FACE",FACE,{"disambiguationData":[OSD([sQuery(id+"F0.wireOp",EDGE,"E5")])],"isStart":false});
            var Q42;
            Q42=makeQuery(id+"F2.opExtrude","CAP_FACE",FACE,{"disambiguationData":[OSD([sQuery(id+"F0.wireOp",EDGE,"E12.29.0")])],"isStart":false});
            var Q43;
            Q43=makeQuery(id+"F2.opExtrude","CAP_FACE",FACE,{"disambiguationData":[OSD([sQuery(id+"F0.wireOp",EDGE,"E11.23.0")])],"isStart":false});
            var Q44;
            Q44=makeQuery(id+"F2.opExtrude","CAP_FACE",FACE,{"disambiguationData":[OSD([sQuery(id+"F0.wireOp",EDGE,"E11.13.0")])],"isStart":false});
            var Q45;
            Q45=makeQuery(id+"F2.opExtrude","CAP_FACE",FACE,{"disambiguationData":[OSD([sQuery(id+"F0.wireOp",EDGE,"E8.2.0")])],"isStart":false});
            var Q46;
            Q46=makeQuery(id+"F2.opExtrude","CAP_FACE",FACE,{"disambiguationData":[OSD([sQuery(id+"F0.wireOp",EDGE,"E8.1.0")])],"isStart":false});
            var Q47;
            Q47=makeQuery(id+"F2.opExtrude","CAP_FACE",FACE,{"disambiguationData":[OSD([sQuery(id+"F0.wireOp",EDGE,"E12.27.0")])],"isStart":false});
            var Q48;
            Q48=makeQuery(id+"F2.opExtrude","CAP_FACE",FACE,{"disambiguationData":[OSD([sQuery(id+"F0.wireOp",EDGE,"E12.18.0")])],"isStart":false});
            var Q49;
            Q49=makeQuery(id+"F2.opExtrude","CAP_FACE",FACE,{"disambiguationData":[OSD([sQuery(id+"F0.wireOp",EDGE,"E11.22.0")])],"isStart":false});
            var Q50;
            Q50=makeQuery(id+"F2.opExtrude","CAP_FACE",FACE,{"disambiguationData":[OSD([sQuery(id+"F0.wireOp",EDGE,"E11.14.0")])],"isStart":false});
            var Q51;
            Q51=makeQuery(id+"F2.opExtrude","CAP_FACE",FACE,{"disambiguationData":[OSD([sQuery(id+"F0.wireOp",EDGE,"E10.17.0")])],"isStart":false});
            var Q52;
            Q52=makeQuery(id+"F2.opExtrude","CAP_FACE",FACE,{"disambiguationData":[OSD([sQuery(id+"F0.wireOp",EDGE,"E10.9.0")])],"isStart":false});
            var Q53;
            Q53=makeQuery(id+"F2.opExtrude","CAP_FACE",FACE,{"disambiguationData":[OSD([sQuery(id+"F0.wireOp",EDGE,"E10.8.0")])],"isStart":false});
            var Q54;
            Q54=makeQuery(id+"F2.opExtrude","CAP_FACE",FACE,{"disambiguationData":[OSD([sQuery(id+"F0.wireOp",EDGE,"E9.6.0")])],"isStart":false});
            var Q55;
            Q55=makeQuery(id+"F2.opExtrude","CAP_FACE",FACE,{"disambiguationData":[OSD([sQuery(id+"F0.wireOp",EDGE,"E9.5.0")])],"isStart":false});
            var Q56;
            Q56=makeQuery(id+"F2.opExtrude","CAP_FACE",FACE,{"disambiguationData":[OSD([sQuery(id+"F0.wireOp",EDGE,"E9.1.0")])],"isStart":false});
            var Q57;
            Q57=makeQuery(id+"F2.opExtrude","CAP_FACE",FACE,{"disambiguationData":[OSD([sQuery(id+"F0.wireOp",EDGE,"E8.5.0")])],"isStart":false});
            var Q58;
            Q58=makeQuery(id+"F2.opExtrude","CAP_FACE",FACE,{"disambiguationData":[OSD([sQuery(id+"F0.wireOp",EDGE,"E8.4.0")])],"isStart":false});
            var Q59;
            Q59=makeQuery(id+"F2.opExtrude","CAP_FACE",FACE,{"disambiguationData":[OSD([sQuery(id+"F0.wireOp",EDGE,"E8.3.0")])],"isStart":false});
            var Q60;
            Q60=makeQuery(id+"F2.opExtrude","CAP_FACE",FACE,{"disambiguationData":[OSD([sQuery(id+"F0.wireOp",EDGE,"E4")])],"isStart":false});
            var Q61;
            Q61=makeQuery(id+"F2.opExtrude","CAP_FACE",FACE,{"disambiguationData":[OSD([sQuery(id+"F0.wireOp",EDGE,"E3")])],"isStart":false});
            var Q62;
            Q62=makeQuery(id+"F2.opExtrude","CAP_FACE",FACE,{"disambiguationData":[OSD([sQuery(id+"F0.wireOp",EDGE,"E2")])],"isStart":false});
            var Q63;
            Q63=makeQuery(id+"F2.opExtrude","CAP_FACE",FACE,{"disambiguationData":[OSD([sQuery(id+"F0.wireOp",EDGE,"E1")])],"isStart":false});
            var Q64;
            Q64=makeQuery(id+"F2.opExtrude","CAP_FACE",FACE,{"disambiguationData":[OSD([sQuery(id+"F0.wireOp",EDGE,"E12.26.0")])],"isStart":false});
            var Q65;
            Q65=makeQuery(id+"F2.opExtrude","CAP_FACE",FACE,{"disambiguationData":[OSD([sQuery(id+"F0.wireOp",EDGE,"E12.19.0")])],"isStart":false});
            var Q66;
            Q66=makeQuery(id+"F2.opExtrude","CAP_FACE",FACE,{"disambiguationData":[OSD([sQuery(id+"F0.wireOp",EDGE,"E11.21.0")])],"isStart":false});
            var Q67;
            Q67=makeQuery(id+"F2.opExtrude","CAP_FACE",FACE,{"disambiguationData":[OSD([sQuery(id+"F0.wireOp",EDGE,"E10.16.0")])],"isStart":false});
            var Q68;
            Q68=makeQuery(id+"F2.opExtrude","CAP_FACE",FACE,{"disambiguationData":[OSD([sQuery(id+"F0.wireOp",EDGE,"E10.14.0")])],"isStart":false});
            var Q69;
            Q69=makeQuery(id+"F2.opExtrude","CAP_FACE",FACE,{"disambiguationData":[OSD([sQuery(id+"F0.wireOp",EDGE,"E10.13.0")])],"isStart":false});
            var Q70;
            Q70=makeQuery(id+"F2.opExtrude","CAP_FACE",FACE,{"disambiguationData":[OSD([sQuery(id+"F0.wireOp",EDGE,"E10.11.0")])],"isStart":false});
            var Q71;
            Q71=makeQuery(id+"F2.opExtrude","CAP_FACE",FACE,{"disambiguationData":[OSD([sQuery(id+"F0.wireOp",EDGE,"E10.10.0")])],"isStart":false});
            var Q72;
            Q72=makeQuery(id+"F2.opExtrude","CAP_FACE",FACE,{"disambiguationData":[OSD([sQuery(id+"F0.wireOp",EDGE,"E9.11.0")])],"isStart":false});
            var Q73;
            Q73=makeQuery(id+"F2.opExtrude","CAP_FACE",FACE,{"disambiguationData":[OSD([sQuery(id+"F0.wireOp",EDGE,"E9.10.0")])],"isStart":false});
            var Q74;
            Q74=makeQuery(id+"F2.opExtrude","CAP_FACE",FACE,{"disambiguationData":[OSD([sQuery(id+"F0.wireOp",EDGE,"E9.9.0")])],"isStart":false});
            var Q75;
            Q75=makeQuery(id+"F2.opExtrude","CAP_FACE",FACE,{"disambiguationData":[OSD([sQuery(id+"F0.wireOp",EDGE,"E9.8.0")])],"isStart":false});
            var Q76;
            Q76=makeQuery(id+"F2.opExtrude","CAP_FACE",FACE,{"disambiguationData":[OSD([sQuery(id+"F0.wireOp",EDGE,"E9.7.0")])],"isStart":false});
            var Q77;
            Q77=makeQuery(id+"F2.opExtrude","CAP_FACE",FACE,{"disambiguationData":[OSD([sQuery(id+"F0.wireOp",EDGE,"E12.25.0")])],"isStart":false});
            var Q78;
            Q78=makeQuery(id+"F2.opExtrude","CAP_FACE",FACE,{"disambiguationData":[OSD([sQuery(id+"F0.wireOp",EDGE,"E12.23.0")])],"isStart":false});
            var Q79;
            Q79=makeQuery(id+"F2.opExtrude","CAP_FACE",FACE,{"disambiguationData":[OSD([sQuery(id+"F0.wireOp",EDGE,"E12.22.0")])],"isStart":false});
            var Q80;
            Q80=makeQuery(id+"F2.opExtrude","CAP_FACE",FACE,{"disambiguationData":[OSD([sQuery(id+"F0.wireOp",EDGE,"E11.20.0")])],"isStart":false});
            var Q81;
            Q81=makeQuery(id+"F2.opExtrude","CAP_FACE",FACE,{"disambiguationData":[OSD([sQuery(id+"F0.wireOp",EDGE,"E11.19.0")])],"isStart":false});
            var Q82;
            Q82=makeQuery(id+"F2.opExtrude","CAP_FACE",FACE,{"disambiguationData":[OSD([sQuery(id+"F0.wireOp",EDGE,"E11.18.0")])],"isStart":false});
            var Q83;
            Q83=makeQuery(id+"F2.opExtrude","CAP_FACE",FACE,{"disambiguationData":[OSD([sQuery(id+"F0.wireOp",EDGE,"E11.17.0")])],"isStart":false});
            var Q84;
            Q84=makeQuery(id+"F2.opExtrude","CAP_FACE",FACE,{"disambiguationData":[OSD([sQuery(id+"F0.wireOp",EDGE,"E11.16.0")])],"isStart":false});
            var Q85;
            Q85=makeQuery(id+"F2.opExtrude","CAP_FACE",FACE,{"disambiguationData":[OSD([sQuery(id+"F0.wireOp",EDGE,"E11.15.0")])],"isStart":false});
            var Q86;
            Q86=makeQuery(id+"F2.opExtrude","CAP_FACE",FACE,{"disambiguationData":[OSD([sQuery(id+"F0.wireOp",EDGE,"E10.15.0")])],"isStart":false});
            var Q87;
            Q87=makeQuery(id+"F2.opExtrude","CAP_FACE",FACE,{"disambiguationData":[OSD([sQuery(id+"F0.wireOp",EDGE,"E10.12.0")])],"isStart":false});
            var Q88;
            Q88=makeQuery(id+"F2.opExtrude","CAP_FACE",FACE,{"disambiguationData":[OSD([sQuery(id+"F0.wireOp",EDGE,"E12.24.0")])],"isStart":false});
            var Q89;
            Q89=makeQuery(id+"F2.opExtrude","CAP_FACE",FACE,{"disambiguationData":[OSD([sQuery(id+"F0.wireOp",EDGE,"E12.21.0")])],"isStart":false});
            var Q90;
            Q90=makeQuery(id+"F2.opExtrude","CAP_FACE",FACE,{"disambiguationData":[OSD([sQuery(id+"F0.wireOp",EDGE,"E12.20.0")])],"isStart":false});
            var Q91;
            Q91=makeQuery(id+"F2.opExtrude","CAP_FACE",FACE,{"disambiguationData":[OSD([sQuery(id+"F0.wireOp",EDGE,"E12.12.0")])],"isStart":true});
            var Q92;
            Q92=makeQuery(id+"F2.opExtrude","CAP_FACE",FACE,{"disambiguationData":[OSD([sQuery(id+"F0.wireOp",EDGE,"E12.8.0")])],"isStart":true});
            var Q93;
            Q93=makeQuery(id+"F2.opExtrude","CAP_FACE",FACE,{"disambiguationData":[OSD([sQuery(id+"F0.wireOp",EDGE,"E12.15.0")])],"isStart":true});
            var Q94;
            Q94=makeQuery(id+"F2.opExtrude","CAP_FACE",FACE,{"disambiguationData":[OSD([sQuery(id+"F0.wireOp",EDGE,"E12.14.0")])],"isStart":true});
            var Q95;
            Q95=makeQuery(id+"F2.opExtrude","CAP_FACE",FACE,{"disambiguationData":[OSD([sQuery(id+"F0.wireOp",EDGE,"E12.11.0")])],"isStart":true});
            var Q96;
            Q96=makeQuery(id+"F2.opExtrude","CAP_FACE",FACE,{"disambiguationData":[OSD([sQuery(id+"F0.wireOp",EDGE,"E12.9.0")])],"isStart":true});
            var Q97;
            Q97=makeQuery(id+"F2.opExtrude","CAP_FACE",FACE,{"disambiguationData":[OSD([sQuery(id+"F0.wireOp",EDGE,"E12.7.0")])],"isStart":true});
            var Q98;
            Q98=makeQuery(id+"F2.opExtrude","CAP_FACE",FACE,{"disambiguationData":[OSD([sQuery(id+"F0.wireOp",EDGE,"E12.6.0")])],"isStart":true});
            var Q99;
            Q99=makeQuery(id+"F2.opExtrude","CAP_FACE",FACE,{"disambiguationData":[OSD([sQuery(id+"F0.wireOp",EDGE,"E12.4.0")])],"isStart":true});
            var Q100;
            Q100=makeQuery(id+"F2.opExtrude","CAP_FACE",FACE,{"disambiguationData":[OSD([sQuery(id+"F0.wireOp",EDGE,"E12.3.0")])],"isStart":true});
            var Q101;
            Q101=makeQuery(id+"F2.opExtrude","CAP_FACE",FACE,{"disambiguationData":[OSD([sQuery(id+"F0.wireOp",EDGE,"E12.1.0")])],"isStart":true});
            var Q102;
            Q102=makeQuery(id+"F2.opExtrude","CAP_FACE",FACE,{"disambiguationData":[OSD([sQuery(id+"F0.wireOp",EDGE,"E6")])],"isStart":true});
            var Q103;
            Q103=makeQuery(id+"F2.opExtrude","CAP_FACE",FACE,{"disambiguationData":[OSD([sQuery(id+"F0.wireOp",EDGE,"E12.13.0")])],"isStart":true});
            var Q104;
            Q104=makeQuery(id+"F2.opExtrude","CAP_FACE",FACE,{"disambiguationData":[OSD([sQuery(id+"F0.wireOp",EDGE,"E12.5.0")])],"isStart":true});
            var Q105;
            Q105=makeQuery(id+"F2.opExtrude","CAP_FACE",FACE,{"disambiguationData":[OSD([sQuery(id+"F0.wireOp",EDGE,"E11.11.0")])],"isStart":true});
            var Q106;
            Q106=makeQuery(id+"F2.opExtrude","CAP_FACE",FACE,{"disambiguationData":[OSD([sQuery(id+"F0.wireOp",EDGE,"E11.10.0")])],"isStart":true});
            var Q107;
            Q107=makeQuery(id+"F2.opExtrude","CAP_FACE",FACE,{"disambiguationData":[OSD([sQuery(id+"F0.wireOp",EDGE,"E11.7.0")])],"isStart":true});
            var Q108;
            Q108=makeQuery(id+"F2.opExtrude","CAP_FACE",FACE,{"disambiguationData":[OSD([sQuery(id+"F0.wireOp",EDGE,"E11.6.0")])],"isStart":true});
            var Q109;
            Q109=makeQuery(id+"F2.opExtrude","CAP_FACE",FACE,{"disambiguationData":[OSD([sQuery(id+"F0.wireOp",EDGE,"E11.2.0")])],"isStart":true});
            var Q110;
            Q110=makeQuery(id+"F2.opExtrude","CAP_FACE",FACE,{"disambiguationData":[OSD([sQuery(id+"F0.wireOp",EDGE,"E12.17.0")])],"isStart":true});
            var Q111;
            Q111=makeQuery(id+"F2.opExtrude","CAP_FACE",FACE,{"disambiguationData":[OSD([sQuery(id+"F0.wireOp",EDGE,"E12.16.0")])],"isStart":true});
            var Q112;
            Q112=makeQuery(id+"F2.opExtrude","CAP_FACE",FACE,{"disambiguationData":[OSD([sQuery(id+"F0.wireOp",EDGE,"E12.10.0")])],"isStart":true});
            var Q113;
            Q113=makeQuery(id+"F2.opExtrude","CAP_FACE",FACE,{"disambiguationData":[OSD([sQuery(id+"F0.wireOp",EDGE,"E12.2.0")])],"isStart":true});
            var Q114;
            Q114=makeQuery(id+"F2.opExtrude","CAP_FACE",FACE,{"disambiguationData":[OSD([sQuery(id+"F0.wireOp",EDGE,"E11.22.0")])],"isStart":true});
            var Q115;
            Q115=makeQuery(id+"F2.opExtrude","CAP_FACE",FACE,{"disambiguationData":[OSD([sQuery(id+"F0.wireOp",EDGE,"E11.12.0")])],"isStart":true});
            var Q116;
            Q116=makeQuery(id+"F2.opExtrude","CAP_FACE",FACE,{"disambiguationData":[OSD([sQuery(id+"F0.wireOp",EDGE,"E11.9.0")])],"isStart":true});
            var Q117;
            Q117=makeQuery(id+"F2.opExtrude","CAP_FACE",FACE,{"disambiguationData":[OSD([sQuery(id+"F0.wireOp",EDGE,"E11.8.0")])],"isStart":true});
            var Q118;
            Q118=makeQuery(id+"F2.opExtrude","CAP_FACE",FACE,{"disambiguationData":[OSD([sQuery(id+"F0.wireOp",EDGE,"E11.5.0")])],"isStart":true});
            var Q119;
            Q119=makeQuery(id+"F2.opExtrude","CAP_FACE",FACE,{"disambiguationData":[OSD([sQuery(id+"F0.wireOp",EDGE,"E11.4.0")])],"isStart":true});
            var Q120;
            Q120=makeQuery(id+"F2.opExtrude","CAP_FACE",FACE,{"disambiguationData":[OSD([sQuery(id+"F0.wireOp",EDGE,"E11.3.0")])],"isStart":true});
            var Q121;
            Q121=makeQuery(id+"F2.opExtrude","CAP_FACE",FACE,{"disambiguationData":[OSD([sQuery(id+"F0.wireOp",EDGE,"E10.5.0")])],"isStart":true});
            var Q122;
            Q122=makeQuery(id+"F2.opExtrude","CAP_FACE",FACE,{"disambiguationData":[OSD([sQuery(id+"F0.wireOp",EDGE,"E12.29.0")])],"isStart":true});
            var Q123;
            Q123=makeQuery(id+"F2.opExtrude","CAP_FACE",FACE,{"disambiguationData":[OSD([sQuery(id+"F0.wireOp",EDGE,"E11.14.0")])],"isStart":true});
            var Q124;
            Q124=makeQuery(id+"F2.opExtrude","CAP_FACE",FACE,{"disambiguationData":[OSD([sQuery(id+"F0.wireOp",EDGE,"E11.13.0")])],"isStart":true});
            var Q125;
            Q125=makeQuery(id+"F2.opExtrude","CAP_FACE",FACE,{"disambiguationData":[OSD([sQuery(id+"F0.wireOp",EDGE,"E11.1.0")])],"isStart":true});
            var Q126;
            Q126=makeQuery(id+"F2.opExtrude","CAP_FACE",FACE,{"disambiguationData":[OSD([sQuery(id+"F0.wireOp",EDGE,"E10.9.0")])],"isStart":true});
            var Q127;
            Q127=makeQuery(id+"F2.opExtrude","CAP_FACE",FACE,{"disambiguationData":[OSD([sQuery(id+"F0.wireOp",EDGE,"E10.6.0")])],"isStart":true});
            var Q128;
            Q128=makeQuery(id+"F2.opExtrude","CAP_FACE",FACE,{"disambiguationData":[OSD([sQuery(id+"F0.wireOp",EDGE,"E10.4.0")])],"isStart":true});
            var Q129;
            Q129=makeQuery(id+"F2.opExtrude","CAP_FACE",FACE,{"disambiguationData":[OSD([sQuery(id+"F0.wireOp",EDGE,"E10.2.0")])],"isStart":true});
            var Q130;
            Q130=makeQuery(id+"F2.opExtrude","CAP_FACE",FACE,{"disambiguationData":[OSD([sQuery(id+"F0.wireOp",EDGE,"E9.4.0")])],"isStart":true});
            var Q131;
            Q131=makeQuery(id+"F2.opExtrude","CAP_FACE",FACE,{"disambiguationData":[OSD([sQuery(id+"F0.wireOp",EDGE,"E4")])],"isStart":true});
            var Q132;
            Q132=makeQuery(id+"F2.opExtrude","CAP_FACE",FACE,{"disambiguationData":[OSD([sQuery(id+"F0.wireOp",EDGE,"E12.28.0")])],"isStart":true});
            var Q133;
            Q133=makeQuery(id+"F2.opExtrude","CAP_FACE",FACE,{"disambiguationData":[OSD([sQuery(id+"F0.wireOp",EDGE,"E12.18.0")])],"isStart":true});
            var Q134;
            Q134=makeQuery(id+"F2.opExtrude","CAP_FACE",FACE,{"disambiguationData":[OSD([sQuery(id+"F0.wireOp",EDGE,"E10.8.0")])],"isStart":true});
            var Q135;
            Q135=makeQuery(id+"F2.opExtrude","CAP_FACE",FACE,{"disambiguationData":[OSD([sQuery(id+"F0.wireOp",EDGE,"E10.7.0")])],"isStart":true});
            var Q136;
            Q136=makeQuery(id+"F2.opExtrude","CAP_FACE",FACE,{"disambiguationData":[OSD([sQuery(id+"F0.wireOp",EDGE,"E10.3.0")])],"isStart":true});
            var Q137;
            Q137=makeQuery(id+"F2.opExtrude","CAP_FACE",FACE,{"disambiguationData":[OSD([sQuery(id+"F0.wireOp",EDGE,"E10.1.0")])],"isStart":true});
            var Q138;
            Q138=makeQuery(id+"F2.opExtrude","CAP_FACE",FACE,{"disambiguationData":[OSD([sQuery(id+"F0.wireOp",EDGE,"E9.5.0")])],"isStart":true});
            var Q139;
            Q139=makeQuery(id+"F2.opExtrude","CAP_FACE",FACE,{"disambiguationData":[OSD([sQuery(id+"F0.wireOp",EDGE,"E9.3.0")])],"isStart":true});
            var Q140;
            Q140=makeQuery(id+"F2.opExtrude","CAP_FACE",FACE,{"disambiguationData":[OSD([sQuery(id+"F0.wireOp",EDGE,"E9.2.0")])],"isStart":true});
            var Q141;
            Q141=makeQuery(id+"F2.opExtrude","CAP_FACE",FACE,{"disambiguationData":[OSD([sQuery(id+"F0.wireOp",EDGE,"E5")])],"isStart":true});
            var Q142;
            Q142=makeQuery(id+"F2.opExtrude","CAP_FACE",FACE,{"disambiguationData":[OSD([sQuery(id+"F0.wireOp",EDGE,"E12.26.0")])],"isStart":true});
            var Q143;
            Q143=makeQuery(id+"F2.opExtrude","CAP_FACE",FACE,{"disambiguationData":[OSD([sQuery(id+"F0.wireOp",EDGE,"E12.19.0")])],"isStart":true});
            var Q144;
            Q144=makeQuery(id+"F2.opExtrude","CAP_FACE",FACE,{"disambiguationData":[OSD([sQuery(id+"F0.wireOp",EDGE,"E11.23.0")])],"isStart":true});
            var Q145;
            Q145=makeQuery(id+"F2.opExtrude","CAP_FACE",FACE,{"disambiguationData":[OSD([sQuery(id+"F0.wireOp",EDGE,"E10.17.0")])],"isStart":true});
            var Q146;
            Q146=makeQuery(id+"F2.opExtrude","CAP_FACE",FACE,{"disambiguationData":[OSD([sQuery(id+"F0.wireOp",EDGE,"E10.16.0")])],"isStart":true});
            var Q147;
            Q147=makeQuery(id+"F2.opExtrude","CAP_FACE",FACE,{"disambiguationData":[OSD([sQuery(id+"F0.wireOp",EDGE,"E10.10.0")])],"isStart":true});
            var Q148;
            Q148=makeQuery(id+"F2.opExtrude","CAP_FACE",FACE,{"disambiguationData":[OSD([sQuery(id+"F0.wireOp",EDGE,"E9.1.0")])],"isStart":true});
            var Q149;
            Q149=makeQuery(id+"F2.opExtrude","CAP_FACE",FACE,{"disambiguationData":[OSD([sQuery(id+"F0.wireOp",EDGE,"E8.3.0")])],"isStart":true});
            var Q150;
            Q150=makeQuery(id+"F2.opExtrude","CAP_FACE",FACE,{"disambiguationData":[OSD([sQuery(id+"F0.wireOp",EDGE,"E8.2.0")])],"isStart":true});
            var Q151;
            Q151=makeQuery(id+"F2.opExtrude","CAP_FACE",FACE,{"disambiguationData":[OSD([sQuery(id+"F0.wireOp",EDGE,"E8.1.0")])],"isStart":true});
            var Q152;
            Q152=makeQuery(id+"F2.opExtrude","CAP_FACE",FACE,{"disambiguationData":[OSD([sQuery(id+"F0.wireOp",EDGE,"E3")])],"isStart":true});
            var Q153;
            Q153=makeQuery(id+"F2.opExtrude","CAP_FACE",FACE,{"disambiguationData":[OSD([sQuery(id+"F0.wireOp",EDGE,"E12.27.0")])],"isStart":true});
            var Q154;
            Q154=makeQuery(id+"F2.opExtrude","CAP_FACE",FACE,{"disambiguationData":[OSD([sQuery(id+"F0.wireOp",EDGE,"E11.15.0")])],"isStart":true});
            var Q155;
            Q155=makeQuery(id+"F2.opExtrude","CAP_FACE",FACE,{"disambiguationData":[OSD([sQuery(id+"F0.wireOp",EDGE,"E9.7.0")])],"isStart":true});
            var Q156;
            Q156=makeQuery(id+"F2.opExtrude","CAP_FACE",FACE,{"disambiguationData":[OSD([sQuery(id+"F0.wireOp",EDGE,"E9.6.0")])],"isStart":true});
            var Q157;
            Q157=makeQuery(id+"F2.opExtrude","CAP_FACE",FACE,{"disambiguationData":[OSD([sQuery(id+"F0.wireOp",EDGE,"E8.5.0")])],"isStart":true});
            var Q158;
            Q158=makeQuery(id+"F2.opExtrude","CAP_FACE",FACE,{"disambiguationData":[OSD([sQuery(id+"F0.wireOp",EDGE,"E2")])],"isStart":true});
            var Q159;
            Q159=makeQuery(id+"F2.opExtrude","CAP_FACE",FACE,{"disambiguationData":[OSD([sQuery(id+"F0.wireOp",EDGE,"E12.25.0")])],"isStart":true});
            var Q160;
            Q160=makeQuery(id+"F2.opExtrude","CAP_FACE",FACE,{"disambiguationData":[OSD([sQuery(id+"F0.wireOp",EDGE,"E11.21.0")])],"isStart":true});
            var Q161;
            Q161=makeQuery(id+"F2.opExtrude","CAP_FACE",FACE,{"disambiguationData":[OSD([sQuery(id+"F0.wireOp",EDGE,"E11.20.0")])],"isStart":true});
            var Q162;
            Q162=makeQuery(id+"F2.opExtrude","CAP_FACE",FACE,{"disambiguationData":[OSD([sQuery(id+"F0.wireOp",EDGE,"E10.12.0")])],"isStart":true});
            var Q163;
            Q163=makeQuery(id+"F2.opExtrude","CAP_FACE",FACE,{"disambiguationData":[OSD([sQuery(id+"F0.wireOp",EDGE,"E10.11.0")])],"isStart":true});
            var Q164;
            Q164=makeQuery(id+"F2.opExtrude","CAP_FACE",FACE,{"disambiguationData":[OSD([sQuery(id+"F0.wireOp",EDGE,"E9.11.0")])],"isStart":true});
            var Q165;
            Q165=makeQuery(id+"F2.opExtrude","CAP_FACE",FACE,{"disambiguationData":[OSD([sQuery(id+"F0.wireOp",EDGE,"E9.8.0")])],"isStart":true});
            var Q166;
            Q166=makeQuery(id+"F2.opExtrude","CAP_FACE",FACE,{"disambiguationData":[OSD([sQuery(id+"F0.wireOp",EDGE,"E8.4.0")])],"isStart":true});
            var Q167;
            Q167=makeQuery(id+"F2.opExtrude","CAP_FACE",FACE,{"disambiguationData":[OSD([sQuery(id+"F0.wireOp",EDGE,"E1")])],"isStart":true});
            var Q168;
            Q168=makeQuery(id+"F2.opExtrude","CAP_FACE",FACE,{"disambiguationData":[OSD([sQuery(id+"F0.wireOp",EDGE,"E12.21.0")])],"isStart":true});
            var Q169;
            Q169=makeQuery(id+"F2.opExtrude","CAP_FACE",FACE,{"disambiguationData":[OSD([sQuery(id+"F0.wireOp",EDGE,"E12.20.0")])],"isStart":true});
            var Q170;
            Q170=makeQuery(id+"F2.opExtrude","CAP_FACE",FACE,{"disambiguationData":[OSD([sQuery(id+"F0.wireOp",EDGE,"E10.14.0")])],"isStart":true});
            var Q171;
            Q171=makeQuery(id+"F2.opExtrude","CAP_FACE",FACE,{"disambiguationData":[OSD([sQuery(id+"F0.wireOp",EDGE,"E10.13.0")])],"isStart":true});
            var Q172;
            Q172=makeQuery(id+"F2.opExtrude","CAP_FACE",FACE,{"disambiguationData":[OSD([sQuery(id+"F0.wireOp",EDGE,"E9.10.0")])],"isStart":true});
            var Q173;
            Q173=makeQuery(id+"F2.opExtrude","CAP_FACE",FACE,{"disambiguationData":[OSD([sQuery(id+"F0.wireOp",EDGE,"E12.24.0")])],"isStart":true});
            var Q174;
            Q174=makeQuery(id+"F2.opExtrude","CAP_FACE",FACE,{"disambiguationData":[OSD([sQuery(id+"F0.wireOp",EDGE,"E11.19.0")])],"isStart":true});
            var Q175;
            Q175=makeQuery(id+"F2.opExtrude","CAP_FACE",FACE,{"disambiguationData":[OSD([sQuery(id+"F0.wireOp",EDGE,"E11.17.0")])],"isStart":true});
            var Q176;
            Q176=makeQuery(id+"F2.opExtrude","CAP_FACE",FACE,{"disambiguationData":[OSD([sQuery(id+"F0.wireOp",EDGE,"E11.16.0")])],"isStart":true});
            var Q177;
            Q177=makeQuery(id+"F2.opExtrude","CAP_FACE",FACE,{"disambiguationData":[OSD([sQuery(id+"F0.wireOp",EDGE,"E10.15.0")])],"isStart":true});
            var Q178;
            Q178=makeQuery(id+"F2.opExtrude","CAP_FACE",FACE,{"disambiguationData":[OSD([sQuery(id+"F0.wireOp",EDGE,"E9.9.0")])],"isStart":true});
            var Q179;
            Q179=makeQuery(id+"F2.opExtrude","CAP_FACE",FACE,{"disambiguationData":[OSD([sQuery(id+"F0.wireOp",EDGE,"E12.23.0")])],"isStart":true});
            var Q180;
            Q180=makeQuery(id+"F2.opExtrude","CAP_FACE",FACE,{"disambiguationData":[OSD([sQuery(id+"F0.wireOp",EDGE,"E12.22.0")])],"isStart":true});
            var Q181;
            Q181=makeQuery(id+"F2.opExtrude","CAP_FACE",FACE,{"disambiguationData":[OSD([sQuery(id+"F0.wireOp",EDGE,"E11.18.0")])],"isStart":true});
            shell(context, id + "F3", {"entities" : qUnion([Q0, Q1, Q2, Q3, Q4, Q5, Q6, Q7, Q8, Q9, Q10, Q11, Q12, Q13, Q14, Q15, Q16, Q17, Q18, Q19, Q20, Q21, Q22, Q23, Q24, Q25, Q26, Q27, Q28, Q29, Q30, Q31, Q32, Q33, Q34, Q35, Q36, Q37, Q38, Q39, Q40, Q41, Q42, Q43, Q44, Q45, Q46, Q47, Q48, Q49, Q50, Q51, Q52, Q53, Q54, Q55, Q56, Q57, Q58, Q59, Q60, Q61, Q62, Q63, Q64, Q65, Q66, Q67, Q68, Q69, Q70, Q71, Q72, Q73, Q74, Q75, Q76, Q77, Q78, Q79, Q80, Q81, Q82, Q83, Q84, Q85, Q86, Q87, Q88, Q89, Q90, Q91, Q92, Q93, Q94, Q95, Q96, Q97, Q98, Q99, Q100, Q101, Q102, Q103, Q104, Q105, Q106, Q107, Q108, Q109, Q110, Q111, Q112, Q113, Q114, Q115, Q116, Q117, Q118, Q119, Q120, Q121, Q122, Q123, Q124, Q125, Q126, Q127, Q128, Q129, Q130, Q131, Q132, Q133, Q134, Q135, Q136, Q137, Q138, Q139, Q140, Q141, Q142, Q143, Q144, Q145, Q146, Q147, Q148, Q149, Q150, Q151, Q152, Q153, Q154, Q155, Q156, Q157, Q158, Q159, Q160, Q161, Q162, Q163, Q164, Q165, Q166, Q167, Q168, Q169, Q170, Q171, Q172, Q173, Q174, Q175, Q176, Q177, Q178, Q179, Q180, Q181]), "thickness" : 1.52 * mm});
        }
        {
            var Q0;
            Q0=makeQuery(id+"F0.imprint","IMPRINT",FACE,{"disambiguationData":[TD([[makeQuery(id+"F0.imprint","IMPRINT",EDGE,{"derivedFrom":sQuery(id+"F0.wireOp",EDGE,"E1")}),-1.0]])]});
            var Q1;
            Q1=makeQuery(id+"F0.imprint","IMPRINT",FACE,{"disambiguationData":[TD([[makeQuery(id+"F0.imprint","IMPRINT",EDGE,{"derivedFrom":sQuery(id+"F0.wireOp",EDGE,"E0")}),1.0]])]});
            extrude(context, id + "F4", {"entities" : qUnion([Q0, Q1]), "depth" : 610.87 * mm, "hasSecondDirection" : true, "secondDirectionOppositeDirection" : false, "secondDirectionDepth" : 609.6 * mm});
        }
        {
            var Q0;
            Q0=makeQuery(id+"F0.imprint","IMPRINT",FACE,{"disambiguationData":[TD([[makeQuery(id+"F0.imprint","IMPRINT",EDGE,{"derivedFrom":sQuery(id+"F0.wireOp",EDGE,"E1")}),-1.0]])]});
            var Q1;
            Q1=makeQuery(id+"F0.imprint","IMPRINT",FACE,{"disambiguationData":[TD([[makeQuery(id+"F0.imprint","IMPRINT",EDGE,{"derivedFrom":sQuery(id+"F0.wireOp",EDGE,"E0")}),1.0]])]});
            extrude(context, id + "F5", {"entities" : qUnion([Q0, Q1]), "oppositeDirection" : true, "depth" : 1.27 * mm});
        }
    });
